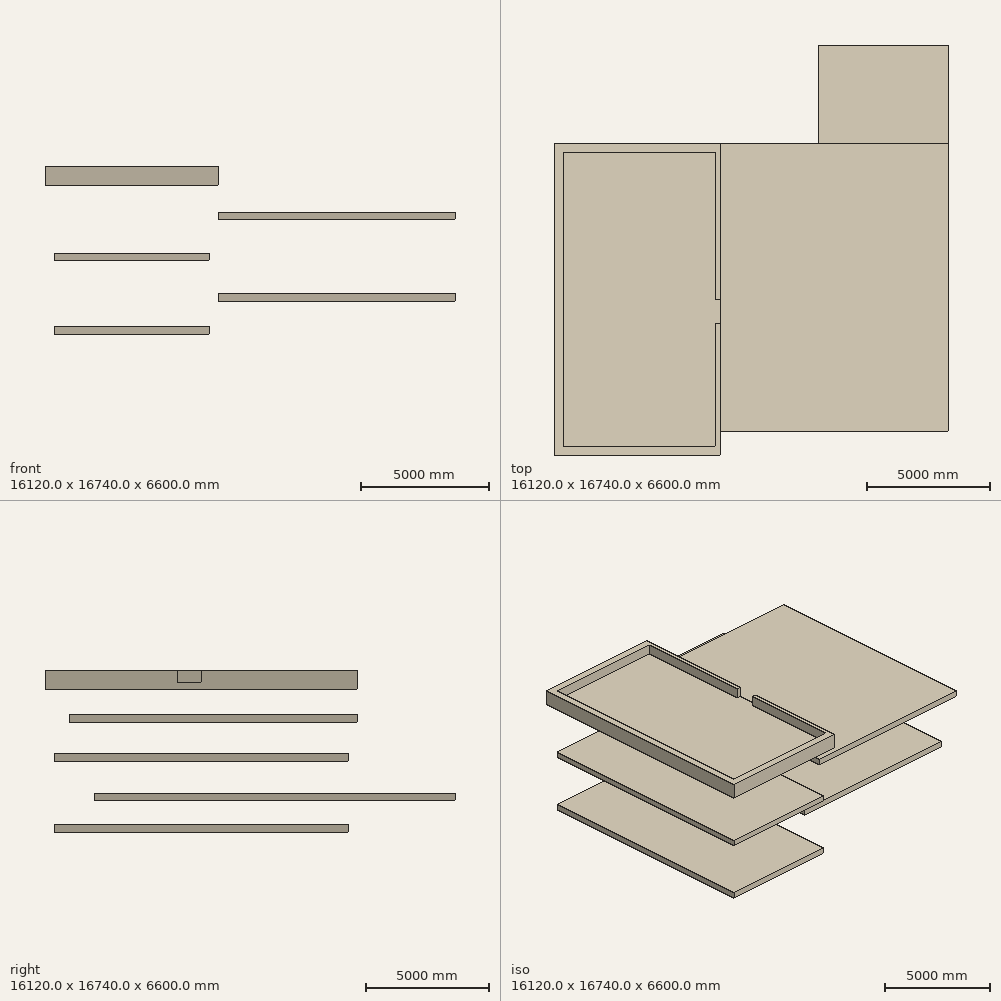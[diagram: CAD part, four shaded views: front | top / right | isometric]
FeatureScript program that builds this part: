
annotation { "Feature Type Name" : "Feature", "Feature Type Description" : "" }
export const myFeature = defineFeature(function(context is Context, id is Id, definition is map)
    precondition{}
    {
        {
            var Q0;
            Q0=qCreatedBy(makeId("Top.planeOp"),FACE);
            var sketch = newSketch(context, id + "F0", { "sketchPlane" : qUnion([Q0])});
            skLineSegment(sketch, "E0.bottom", {"start": v(0, 6370) * mm, "end": v(0, 6370) * mm});
            skLineSegment(sketch, "E0.top", {"start": v(0, -6370) * mm, "end": v(0, -6370) * mm});
            skLineSegment(sketch, "E0.left", {"start": v(0, 6370) * mm, "end": v(0, -6370) * mm});
            skLineSegment(sketch, "E0.right", {"start": v(0, 6370) * mm, "end": v(0, 0) * mm});
            skLineSegment(sketch, "E1", {"start": v(0, -6370) * mm, "end": v(-6810, -6370) * mm});
            skLineSegment(sketch, "E2", {"start": v(-6810, -6370) * mm, "end": v(-6810, 6370) * mm});
            skLineSegment(sketch, "E3", {"start": v(-6810, 6370) * mm, "end": v(-6810, 6370) * mm});
            skLineSegment(sketch, "E4", {"start": v(-6810, 6370) * mm, "end": v(0, 6370) * mm});
            skLineSegment(sketch, "E5.0", {"start": v(-6435, 5995) * mm, "end": v(-200, 5995) * mm});
            skLineSegment(sketch, "E5.1", {"start": v(-6435, -5995) * mm, "end": v(-6435, 5995) * mm});
            skLineSegment(sketch, "E5.2", {"start": v(-200, -5995) * mm, "end": v(-6435, -5995) * mm});
            skLineSegment(sketch, "E6.0", {"start": v(-200, 5995) * mm, "end": v(-200, 0) * mm});
            skLineSegment(sketch, "E7", {"start": v(-200, -1000) * mm, "end": v(0, -1000) * mm});
            skLineSegment(sketch, "E8", {"start": v(-200, 0) * mm, "end": v(0, 0) * mm});
            skLineSegment(sketch, "E9.trimOffspring", {"start": v(-200, -1000) * mm, "end": v(-200, -5995) * mm});
            skLineSegment(sketch, "E10.trimOffspring", {"start": v(0, -1000) * mm, "end": v(0, -6370) * mm});
            skSolve(sketch);
        }
        {
            var Q0;
            {var subQ0=sQuery(id+"F0.wireOp",EDGE,"E1");Q0=makeQuery(id+"F0.imprint","IMPRINT",FACE,{"disambiguationData":[TD([[makeQuery(id+"F0.imprint","IMPRINT",EDGE,{"derivedFrom":subQ0}),-1.0]])]});}
            extrude(context, id + "F1", {"entities" : qUnion([Q0]), "depth" : 500 * mm});
        }
        {
            var Q0;
            Q0=qCreatedBy(makeId("Top.planeOp"),FACE);
            var sketch = newSketch(context, id + "F2", { "sketchPlane" : qUnion([Q0])});
            skLineSegment(sketch, "E11.bottom", {"start": v(0, 6370) * mm, "end": v(-6810, 6370) * mm});
            skLineSegment(sketch, "E11.top", {"start": v(0, -6370) * mm, "end": v(-6810, -6370) * mm});
            skLineSegment(sketch, "E11.left", {"start": v(0, 6370) * mm, "end": v(0, -6370) * mm});
            skLineSegment(sketch, "E11.right", {"start": v(-6810, 6370) * mm, "end": v(-6810, -6370) * mm});
            skSolve(sketch);
        }
        {
            var Q0;
            Q0 = qSketchRegion(id + "F2", true);
            extrude(context, id + "F3", {"entities" : qUnion([Q0]), "operationType" : NewBodyOperationType.ADD, "oppositeDirection" : true, "depth" : 250 * mm});
        }
        {
            var Q0;
            Q0=qCreatedBy(makeId("Top.planeOp"),FACE);
            var sketch = newSketch(context, id + "F4", { "sketchPlane" : qUnion([Q0])});
            skLineSegment(sketch, "E12.bottom", {"start": v(-6810, -6370) * mm, "end": v(0, -6370) * mm});
            skLineSegment(sketch, "E12.top", {"start": v(-6810, 6370) * mm, "end": v(0, 6370) * mm});
            skLineSegment(sketch, "E12.left", {"start": v(-6810, 6370) * mm, "end": v(-6810, -6370) * mm});
            skLineSegment(sketch, "E12.right", {"start": v(0, 6370) * mm, "end": v(0, -6370) * mm});
            skLineSegment(sketch, "E13.0", {"start": v(-6445, 6005) * mm, "end": v(-6445, -6005) * mm});
            skLineSegment(sketch, "E13.1", {"start": v(-6445, 6005) * mm, "end": v(-365, 6005) * mm});
            skLineSegment(sketch, "E13.2", {"start": v(-365, 6005) * mm, "end": v(-365, -6005) * mm});
            skLineSegment(sketch, "E13.3", {"start": v(-6445, -6005) * mm, "end": v(-365, -6005) * mm});
            skSolve(sketch);
        }
        {
            var Q0;
            Q0=qCreatedBy(makeId("Top.planeOp"),FACE);
            cPlane(context, id + "F5", {"entities" : qUnion([Q0]), "cplaneType" : CPlaneType.OFFSET, "offset" : 2900 * mm, "oppositeDirection" : true, "width" : 150 * mm, "height" : 150 * mm});
        }
        {
            var Q0;
            Q0=qCreatedBy(id+"F5.planeOp",FACE);
            var sketch = newSketch(context, id + "F6", { "sketchPlane" : qUnion([Q0])});
            skLineSegment(sketch, "E14.0", {"start": v(-365, 6005) * mm, "end": v(-365, -6005) * mm});
            skLineSegment(sketch, "E15.0", {"start": v(-365, -6005) * mm, "end": v(-365, -6005) * mm});
            skLineSegment(sketch, "E16.0", {"start": v(-365, 6005) * mm, "end": v(-365, 6005) * mm});
            skLineSegment(sketch, "E17.0.0", {"start": v(-6445, 6005) * mm, "end": v(-6445, -6005) * mm});
            skLineSegment(sketch, "E17.0.1", {"start": v(-6445, -6005) * mm, "end": v(-365, -6005) * mm});
            skLineSegment(sketch, "E17.0.2", {"start": v(-365, -6005) * mm, "end": v(-365, 6005) * mm});
            skLineSegment(sketch, "E17.0.3", {"start": v(-365, 6005) * mm, "end": v(-6445, 6005) * mm});
            skSolve(sketch);
        }
        {
            var Q0;
            Q0 = qSketchRegion(id + "F6", true);
            extrude(context, id + "F7", {"entities" : qUnion([Q0]), "operationType" : NewBodyOperationType.ADD, "oppositeDirection" : true, "depth" : 300 * mm});
        }
        {
            var Q0;
            Q0=makeQuery(id+"F7.opExtrude","CAP_FACE",FACE,{"disambiguationData":[OSD([sQuery(id+"F6.wireOp",EDGE,"E17.0.0"),sQuery(id+"F6.wireOp",EDGE,"E17.0.1"),sQuery(id+"F6.wireOp",EDGE,"E17.0.2"),sQuery(id+"F6.wireOp",EDGE,"E17.0.3")])],"isStart":false});
            cPlane(context, id + "F8", {"entities" : qUnion([Q0]), "cplaneType" : CPlaneType.OFFSET, "offset" : 2600 * mm, "width" : 150 * mm, "height" : 150 * mm});
        }
        {
            var Q0;
            Q0=qCreatedBy(id+"F8.planeOp",FACE);
            var sketch = newSketch(context, id + "F9", { "sketchPlane" : qUnion([Q0])});
            skLineSegment(sketch, "E18.0.0", {"start": v(-365, -6005) * mm, "end": v(-365, 6005) * mm});
            skLineSegment(sketch, "E18.0.1", {"start": v(-365, 6005) * mm, "end": v(-6445, 6005) * mm});
            skLineSegment(sketch, "E18.0.2", {"start": v(-6445, 6005) * mm, "end": v(-6445, -6005) * mm});
            skLineSegment(sketch, "E18.0.3", {"start": v(-6445, -6005) * mm, "end": v(-365, -6005) * mm});
            skSolve(sketch);
        }
        {
            var Q0;
            Q0=makeQuery(id+"F9.imprint","IMPRINT",FACE,{"disambiguationData":[TD([[makeQuery(id+"F9.imprint","IMPRINT",EDGE,{"derivedFrom":sQuery(id+"F9.wireOp",EDGE,"E18.0.0")}),1.0]])]});
            extrude(context, id + "F10", {"entities" : qUnion([Q0]), "depth" : 300 * mm});
        }
        {
            var Q0;
            Q0=makeQuery(id+"F6.imprint","IMPRINT",FACE,{"disambiguationData":[TD([[makeQuery(id+"F6.imprint","IMPRINT",EDGE,{"derivedFrom":sQuery(id+"F6.wireOp",EDGE,"E17.0.0")}),1.0]])]});
            cPlane(context, id + "F11", {"entities" : qUnion([Q0]), "cplaneType" : CPlaneType.OFFSET, "offset" : 1600 * mm, "oppositeDirection" : true, "width" : 150 * mm, "height" : 150 * mm});
        }
        {
            var Q0;
            Q0=qCreatedBy(id+"F11.planeOp",FACE);
            var sketch = newSketch(context, id + "F12", { "sketchPlane" : qUnion([Q0])});
            skLineSegment(sketch, "E19.0", {"start": v(0, 6370) * mm, "end": v(0, 6370) * mm});
            skLineSegment(sketch, "E20.0", {"start": v(0, 4870) * mm, "end": v(0, -6370) * mm});
            skLineSegment(sketch, "E21", {"start": v(4000, 4870) * mm, "end": v(4000, 10370) * mm});
            skLineSegment(sketch, "E22", {"start": v(4000, 10370) * mm, "end": v(9310, 10370) * mm});
            skLineSegment(sketch, "E23", {"start": v(9310, 10370) * mm, "end": v(9310, -4370) * mm});
            skLineSegment(sketch, "E24", {"start": v(9310, -4370) * mm, "end": v(0, -4370) * mm});
            skLineSegment(sketch, "E25", {"start": v(0, 4870) * mm, "end": v(4000, 4870) * mm});
            skSolve(sketch);
        }
        {
            var Q0;
            Q0=makeQuery(id+"F12.imprint","IMPRINT",FACE,{"disambiguationData":[TD([[makeQuery(id+"F12.imprint","IMPRINT",EDGE,{"derivedFrom":sQuery(id+"F12.wireOp",EDGE,"E19.0")}),1.0]])]});
            var Q1;
            Q1=makeQuery(id+"F12.imprint","IMPRINT",FACE,{"disambiguationData":[TD([[makeQuery(id+"F12.imprint","IMPRINT",EDGE,{"derivedFrom":sQuery(id+"F12.wireOp",EDGE,"E21")}),-1.0]])]});
            extrude(context, id + "F13", {"entities" : qUnion([Q0, Q1]), "oppositeDirection" : true, "depth" : 300 * mm});
        }
        {
            var Q0;
            Q0=makeQuery(id+"F4.imprint","IMPRINT",FACE,{"disambiguationData":[TD([[makeQuery(id+"F4.imprint","IMPRINT",EDGE,{"derivedFrom":sQuery(id+"F4.wireOp",EDGE,"E13.0")}),1.0]])]});
            cPlane(context, id + "F14", {"entities" : qUnion([Q0]), "cplaneType" : CPlaneType.OFFSET, "offset" : 1300 * mm, "oppositeDirection" : true, "width" : 150 * mm, "height" : 150 * mm});
        }
        {
            var Q0;
            Q0=qCreatedBy(id+"F14.planeOp",FACE);
            var sketch = newSketch(context, id + "F15", { "sketchPlane" : qUnion([Q0])});
            skLineSegment(sketch, "E26.0.0", {"start": v(9310, -5370) * mm, "end": v(9310, 6370) * mm});
            skLineSegment(sketch, "E26.0.4", {"start": v(0, 6370) * mm, "end": v(0, -5370) * mm});
            skLineSegment(sketch, "E26.0.5", {"start": v(0, -5370) * mm, "end": v(9310, -5370) * mm});
            skPoint(sketch, "E26.0.1.end.orphan", {"position": v(4000, 10370) * mm});
            skPoint(sketch, "E27.orphan", {"position": v(9310, 10370) * mm});
            skPoint(sketch, "E28.end.orphan", {"position": v(0, 6370) * mm});
            skLineSegment(sketch, "E29", {"start": v(0, 6370) * mm, "end": v(9310, 6370) * mm});
            skSolve(sketch);
        }
        {
            var Q0;
            Q0=makeQuery(id+"F15.imprint","IMPRINT",FACE,{"disambiguationData":[TD([[makeQuery(id+"F15.imprint","IMPRINT",EDGE,{"derivedFrom":sQuery(id+"F15.wireOp",EDGE,"E26.0.3")}),1.0]])]});
            var Q1;
            Q1=makeQuery(id+"F15.imprint","IMPRINT",FACE,{"disambiguationData":[TD([[makeQuery(id+"F15.imprint","IMPRINT",EDGE,{"derivedFrom":sQuery(id+"F15.wireOp",EDGE,"E26.0.0")}),1.0]])]});
            extrude(context, id + "F16", {"entities" : qUnion([Q0, Q1]), "oppositeDirection" : true, "depth" : 300 * mm});
        }
    });
